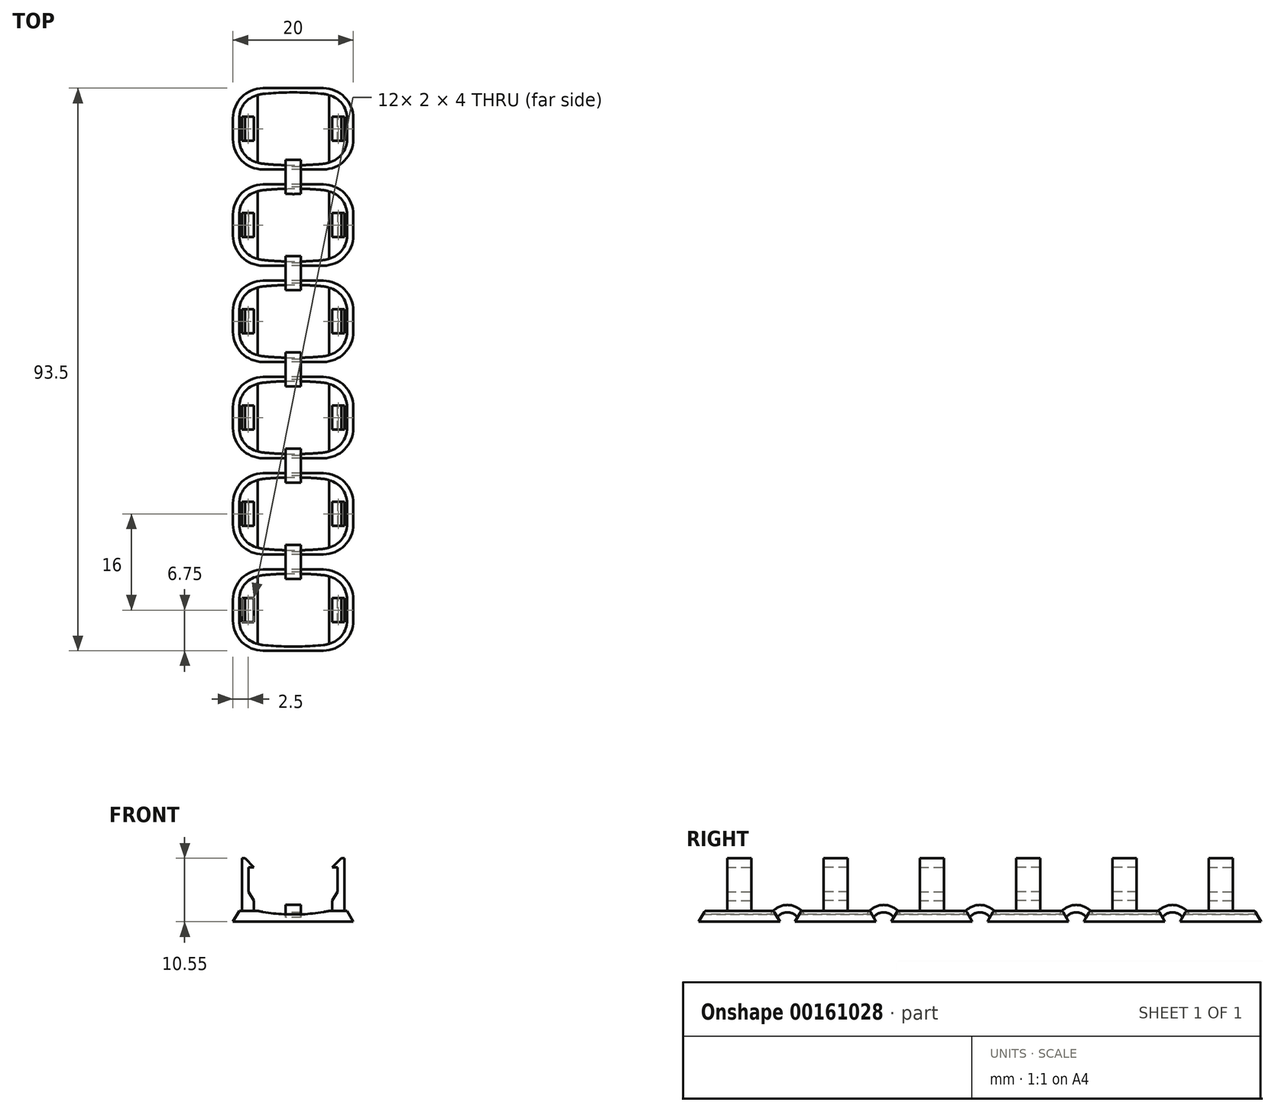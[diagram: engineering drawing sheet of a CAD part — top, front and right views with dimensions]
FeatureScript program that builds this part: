
annotation { "Feature Type Name" : "Feature", "Feature Type Description" : "" }
export const myFeature = defineFeature(function(context is Context, id is Id, definition is map)
    precondition{}
    {
        {
            var Q0;
            Q0=qCreatedBy(makeId("Top.planeOp"),FACE);
            var sketch = newSketch(context, id + "F0", { "sketchPlane" : qUnion([Q0])});
            skLineSegment(sketch, "E0.bottom", {"start": v(-5, 6.75) * mm, "end": v(5, 6.75) * mm});
            skLineSegment(sketch, "E0.top", {"start": v(-5, -6.75) * mm, "end": v(5, -6.75) * mm});
            skLineSegment(sketch, "E0.left", {"start": v(-10, 1.75) * mm, "end": v(-10, -1.75) * mm});
            skLineSegment(sketch, "E0.right", {"start": v(10, 1.75) * mm, "end": v(10, -1.75) * mm});
            skLineSegment(sketch, "E1", {"start": v(0, 21.6) * mm, "end": v(0, 6.75) * mm, "construction": true});
            skLineSegment(sketch, "E2", {"start": v(-21.62, 0) * mm, "end": v(-10, 0) * mm, "construction": true});
            skArc(sketch, "E3", {"start": v(-5, 6.75) * mm, "mid": v(-8.54, 5.29) * mm, "end": v(-10, 1.75) * mm});
            skArc(sketch, "E4", {"start": v(10, 1.75) * mm, "mid": v(8.54, 5.29) * mm, "end": v(5, 6.75) * mm});
            skArc(sketch, "E5", {"start": v(5, -6.75) * mm, "mid": v(8.54, -5.29) * mm, "end": v(10, -1.75) * mm});
            skPoint(sketch, "E6.orphan", {"position": v(10, 6.75) * mm});
            skArc(sketch, "E7.trimOffspring", {"start": v(-10, -1.75) * mm, "mid": v(-8.54, -5.29) * mm, "end": v(-5, -6.75) * mm});
            skLineSegment(sketch, "E8.trimOffspring", {"start": v(10, 0) * mm, "end": v(28.3, 0) * mm, "construction": true});
            skLineSegment(sketch, "E9.trimOffspring", {"start": v(0, -6.75) * mm, "end": v(0, -26.74) * mm, "construction": true});
            skSolve(sketch);
        }
        {
            var Q0;
            Q0=makeQuery(id+"F0.imprint","IMPRINT",FACE,{"disambiguationData":[TD([[makeQuery(id+"F0.imprint","IMPRINT",EDGE,{"derivedFrom":sQuery(id+"F0.wireOp",EDGE,"E0.bottom")}),-1.0]])]});
            extrude(context, id + "F1", {"entities" : qUnion([Q0]), "depth" : 1.8 * mm});
        }
        {
            var Q0;
            Q0=makeQuery(id+"F1.opExtrude","CAP_EDGE",EDGE,{"disambiguationData":[OSD([sQuery(id+"F0.wireOp",EDGE,"E0.top")])],"isStart":false});
            var Q1;
            Q1=makeQuery(id+"F1.opExtrude","CAP_EDGE",EDGE,{"disambiguationData":[OSD([sQuery(id+"F0.wireOp",EDGE,"E7.trimOffspring")])],"isStart":false});
            var Q2;
            Q2=makeQuery(id+"F1.opExtrude","CAP_EDGE",EDGE,{"disambiguationData":[OSD([sQuery(id+"F0.wireOp",EDGE,"E0.right")])],"isStart":false});
            var Q3;
            Q3=makeQuery(id+"F1.opExtrude","CAP_EDGE",EDGE,{"disambiguationData":[OSD([sQuery(id+"F0.wireOp",EDGE,"E5")])],"isStart":false});
            var Q4;
            Q4=makeQuery(id+"F1.opExtrude","CAP_EDGE",EDGE,{"disambiguationData":[OSD([sQuery(id+"F0.wireOp",EDGE,"E4")])],"isStart":false});
            var Q5;
            Q5=makeQuery(id+"F1.opExtrude","CAP_EDGE",EDGE,{"disambiguationData":[OSD([sQuery(id+"F0.wireOp",EDGE,"E0.bottom")])],"isStart":false});
            var Q6;
            Q6=makeQuery(id+"F1.opExtrude","CAP_EDGE",EDGE,{"disambiguationData":[OSD([sQuery(id+"F0.wireOp",EDGE,"E3")])],"isStart":false});
            var Q7;
            Q7=makeQuery(id+"F1.opExtrude","CAP_EDGE",EDGE,{"disambiguationData":[OSD([sQuery(id+"F0.wireOp",EDGE,"E0.left")])],"isStart":false});
            chamfer(context, id + "F2", {"entities" : qUnion([Q0, Q1, Q2, Q3, Q4, Q5, Q6, Q7]), "chamferType" : ChamferType.OFFSET_ANGLE, "width" : 1.04 * mm, "oppositeDirection" : false, "angle" : 60 * degree, "tangentPropagation" : true});
        }
        {
            var Q0;
            Q0=qCreatedBy(makeId("Front.planeOp"),FACE);
            var sketch = newSketch(context, id + "F3", { "sketchPlane" : qUnion([Q0])});
            skLineSegment(sketch, "E10", {"start": v(-6, 4.57) * mm, "end": v(-6, -3.38) * mm, "construction": true});
            skLineSegment(sketch, "E11", {"start": v(6, 4.53) * mm, "end": v(6, -3.32) * mm, "construction": true});
            skLineSegment(sketch, "E12", {"start": v(-10.74, 1.2) * mm, "end": v(11.87, 1.2) * mm, "construction": true});
            skArc(sketch, "E13", {"start": v(-6, 1.83) * mm, "mid": v(0, 1.2) * mm, "end": v(6, 1.8) * mm});
            skLineSegment(sketch, "E14", {"start": v(-6, 1.83) * mm, "end": v(-6, 3.37) * mm});
            skLineSegment(sketch, "E15", {"start": v(-6, 3.37) * mm, "end": v(6, 3.37) * mm});
            skLineSegment(sketch, "E16", {"start": v(6, 3.37) * mm, "end": v(6, 1.8) * mm});
            skSolve(sketch);
        }
        {
            var Q0;
            Q0 = qSketchRegion(id + "F3", true);
            extrude(context, id + "F4", {"entities" : qUnion([Q0]), "operationType" : NewBodyOperationType.REMOVE, "endBound" : BoundingType.SYMMETRIC, "oppositeDirection" : true, "depth" : 25 * mm});
        }
        {
            var Q0;
            Q0=qCreatedBy(makeId("Front.planeOp"),FACE);
            var sketch = newSketch(context, id + "F5", { "sketchPlane" : qUnion([Q0])});
            skLineSegment(sketch, "E17", {"start": v(-8.5, 11.85) * mm, "end": v(-8.5, 10.55) * mm, "construction": true});
            skLineSegment(sketch, "E18", {"start": v(8.5, 11.72) * mm, "end": v(8.5, -3.28) * mm, "construction": true});
            skLineSegment(sketch, "E19", {"start": v(-6.5, 11.8) * mm, "end": v(-6.5, -3.2) * mm, "construction": true});
            skLineSegment(sketch, "E20", {"start": v(6.5, 11.8) * mm, "end": v(6.5, -3.2) * mm, "construction": true});
            skLineSegment(sketch, "E21", {"start": v(-10.2, 10.55) * mm, "end": v(9.76, 10.55) * mm, "construction": true});
            skLineSegment(sketch, "E22", {"start": v(-11.42, 3.5) * mm, "end": v(12.16, 3.5) * mm, "construction": true});
            skLineSegment(sketch, "E23", {"start": v(-11.49, 5) * mm, "end": v(12.2, 5) * mm, "construction": true});
            skLineSegment(sketch, "E24", {"start": v(-7.4, 11.84) * mm, "end": v(-7.4, -3.13) * mm, "construction": true});
            skLineSegment(sketch, "E25", {"start": v(7.4, 11.66) * mm, "end": v(7.4, -3.03) * mm, "construction": true});
            skLineSegment(sketch, "E26", {"start": v(-11.03, 9.05) * mm, "end": v(14.92, 9.05) * mm, "construction": true});
            skLineSegment(sketch, "E27.top", {"start": v(-8.5, 10.55) * mm, "end": v(-8.5, 10.55) * mm});
            skLineSegment(sketch, "E28.trimOffspring", {"start": v(-8.5, 1.8) * mm, "end": v(-8.5, -3.15) * mm, "construction": true});
            skLineSegment(sketch, "E29", {"start": v(-8.5, 10.55) * mm, "end": v(-8.5, 1.8) * mm, "construction": true});
            skLineSegment(sketch, "E30", {"start": v(-8.5, 1.8) * mm, "end": v(-8.5, 10.55) * mm});
            skLineSegment(sketch, "E31", {"start": v(-8.5, 10.55) * mm, "end": v(-8, 10.55) * mm});
            skLineSegment(sketch, "E32", {"start": v(-6.5, 9.05) * mm, "end": v(-7.4, 9.05) * mm});
            skLineSegment(sketch, "E33", {"start": v(-7.4, 9.05) * mm, "end": v(-6.5, 9.05) * mm});
            skLineSegment(sketch, "E34", {"start": v(-7.4, 9.05) * mm, "end": v(-7.4, 5) * mm});
            skLineSegment(sketch, "E35", {"start": v(-7.4, 5) * mm, "end": v(-6.5, 3.5) * mm});
            skLineSegment(sketch, "E36", {"start": v(-6.5, 3.5) * mm, "end": v(-6.5, 1.79) * mm});
            skLineSegment(sketch, "E37", {"start": v(-6.5, 1.79) * mm, "end": v(-8.5, 1.8) * mm});
            skLineSegment(sketch, "E38", {"start": v(6.5, 1.8) * mm, "end": v(6.5, 3.5) * mm});
            skLineSegment(sketch, "E39", {"start": v(6.5, 3.5) * mm, "end": v(7.4, 5) * mm});
            skLineSegment(sketch, "E40", {"start": v(7.4, 5) * mm, "end": v(7.4, 9.05) * mm});
            skLineSegment(sketch, "E41", {"start": v(7.4, 9.05) * mm, "end": v(6.5, 9.05) * mm});
            skLineSegment(sketch, "E42", {"start": v(6.5, 9.05) * mm, "end": v(8, 10.55) * mm});
            skLineSegment(sketch, "E43", {"start": v(8, 10.55) * mm, "end": v(8.5, 10.55) * mm});
            skLineSegment(sketch, "E44", {"start": v(8.5, 10.55) * mm, "end": v(8.5, 1.8) * mm});
            skLineSegment(sketch, "E45", {"start": v(8.5, 1.8) * mm, "end": v(6.5, 1.8) * mm});
            skLineSegment(sketch, "E46", {"start": v(-8, 10.55) * mm, "end": v(-6.5, 9.05) * mm});
            skSolve(sketch);
        }
        {
            var Q0;
            Q0 = qSketchRegion(id + "F5", true);
            extrude(context, id + "F6", {"entities" : qUnion([Q0]), "operationType" : NewBodyOperationType.ADD, "endBound" : BoundingType.SYMMETRIC, "depth" : 4 * mm});
        }
        {
            var Q0;
            Q0=qCreatedBy(makeId("Front.planeOp"),FACE);
            cPlane(context, id + "F7", {"entities" : qUnion([Q0]), "cplaneType" : CPlaneType.OFFSET, "offset" : 8 * mm, "width" : 150 * mm, "height" : 150 * mm});
        }
        {
            var Q0;
            Q0=makeQuery(id+"F1.opExtrude","SWEPT_BODY",BODY,{"disambiguationData":[OSD([sQuery(id+"F0.wireOp",EDGE,"E0.bottom"),sQuery(id+"F0.wireOp",EDGE,"E0.top"),sQuery(id+"F0.wireOp",EDGE,"E0.left"),sQuery(id+"F0.wireOp",EDGE,"E0.right"),sQuery(id+"F0.wireOp",EDGE,"E3"),sQuery(id+"F0.wireOp",EDGE,"E4"),sQuery(id+"F0.wireOp",EDGE,"E5"),sQuery(id+"F0.wireOp",EDGE,"E7.trimOffspring")])]});
            var Q1;
            Q1=qCreatedBy(id+"F7.planeOp",FACE);
            mirror(context, id + "F8", {"entities" : qUnion([Q0]), "mirrorPlane" : qUnion([Q1])});
        }
        {
            var Q0;
            Q0=qCreatedBy(id+"F7.planeOp",FACE);
            cPlane(context, id + "F9", {"entities" : qUnion([Q0]), "cplaneType" : CPlaneType.OFFSET, "offset" : 16 * mm, "width" : 150 * mm, "height" : 150 * mm});
        }
        {
            var Q0;
            Q0=makeQuery(id+"F8.opPattern","COPY",BODY,{"derivedFrom":makeQuery(id+"F1.opExtrude","SWEPT_BODY",BODY,{"disambiguationData":[OSD([sQuery(id+"F0.wireOp",EDGE,"E0.bottom"),sQuery(id+"F0.wireOp",EDGE,"E0.top"),sQuery(id+"F0.wireOp",EDGE,"E0.left"),sQuery(id+"F0.wireOp",EDGE,"E0.right"),sQuery(id+"F0.wireOp",EDGE,"E3"),sQuery(id+"F0.wireOp",EDGE,"E4"),sQuery(id+"F0.wireOp",EDGE,"E5"),sQuery(id+"F0.wireOp",EDGE,"E7.trimOffspring")])]}),"instanceName":"1"});
            var Q1;
            Q1=qCreatedBy(id+"F9.planeOp",FACE);
            mirror(context, id + "F10", {"entities" : qUnion([Q0]), "mirrorPlane" : qUnion([Q1])});
        }
        {
            var Q0;
            Q0=qCreatedBy(makeId("Front.planeOp"),FACE);
            cPlane(context, id + "F11", {"entities" : qUnion([Q0]), "cplaneType" : CPlaneType.OFFSET, "offset" : 8 * mm, "oppositeDirection" : true, "width" : 150 * mm, "height" : 150 * mm});
        }
        {
            var Q0;
            Q0=makeQuery(id+"F1.opExtrude","SWEPT_BODY",BODY,{"disambiguationData":[OSD([sQuery(id+"F0.wireOp",EDGE,"E0.bottom"),sQuery(id+"F0.wireOp",EDGE,"E0.top"),sQuery(id+"F0.wireOp",EDGE,"E0.left"),sQuery(id+"F0.wireOp",EDGE,"E0.right"),sQuery(id+"F0.wireOp",EDGE,"E3"),sQuery(id+"F0.wireOp",EDGE,"E4"),sQuery(id+"F0.wireOp",EDGE,"E5"),sQuery(id+"F0.wireOp",EDGE,"E7.trimOffspring")])]});
            var Q1;
            Q1=makeQuery(id+"F8.opPattern","COPY",BODY,{"derivedFrom":makeQuery(id+"F1.opExtrude","SWEPT_BODY",BODY,{"disambiguationData":[OSD([sQuery(id+"F0.wireOp",EDGE,"E0.bottom"),sQuery(id+"F0.wireOp",EDGE,"E0.top"),sQuery(id+"F0.wireOp",EDGE,"E0.left"),sQuery(id+"F0.wireOp",EDGE,"E0.right"),sQuery(id+"F0.wireOp",EDGE,"E3"),sQuery(id+"F0.wireOp",EDGE,"E4"),sQuery(id+"F0.wireOp",EDGE,"E5"),sQuery(id+"F0.wireOp",EDGE,"E7.trimOffspring")])]}),"instanceName":"1"});
            var Q2;
            Q2=makeQuery(id+"F10.opPattern","COPY",BODY,{"derivedFrom":makeQuery(id+"F1.opExtrude","SWEPT_BODY",BODY,{"disambiguationData":[OSD([sQuery(id+"F0.wireOp",EDGE,"E0.bottom"),sQuery(id+"F0.wireOp",EDGE,"E0.top"),sQuery(id+"F0.wireOp",EDGE,"E0.left"),sQuery(id+"F0.wireOp",EDGE,"E0.right"),sQuery(id+"F0.wireOp",EDGE,"E3"),sQuery(id+"F0.wireOp",EDGE,"E4"),sQuery(id+"F0.wireOp",EDGE,"E5"),sQuery(id+"F0.wireOp",EDGE,"E7.trimOffspring")])]}),"instanceName":"1"});
            var Q3;
            Q3=makeQuery(id+"F10.opPattern","COPY",BODY,{"derivedFrom":makeQuery(id+"F8.opPattern","COPY",BODY,{"derivedFrom":makeQuery(id+"F1.opExtrude","SWEPT_BODY",BODY,{"disambiguationData":[OSD([sQuery(id+"F0.wireOp",EDGE,"E0.bottom"),sQuery(id+"F0.wireOp",EDGE,"E0.top"),sQuery(id+"F0.wireOp",EDGE,"E0.left"),sQuery(id+"F0.wireOp",EDGE,"E0.right"),sQuery(id+"F0.wireOp",EDGE,"E3"),sQuery(id+"F0.wireOp",EDGE,"E4"),sQuery(id+"F0.wireOp",EDGE,"E5"),sQuery(id+"F0.wireOp",EDGE,"E7.trimOffspring")])]}),"instanceName":"1"}),"instanceName":"1"});
            var Q4;
            Q4=qCreatedBy(id+"F11.planeOp",FACE);
            mirror(context, id + "F12", {"entities" : qUnion([Q0, Q1, Q2, Q3]), "mirrorPlane" : qUnion([Q4])});
        }
        {
            var Q0;
            Q0=qCreatedBy(makeId("Right.planeOp"),FACE);
            var sketch = newSketch(context, id + "F13", { "sketchPlane" : qUnion([Q0])});
            skLineSegment(sketch, "E47", {"start": v(-11.94, 1.3) * mm, "end": v(-4.48, 1.3) * mm, "construction": true});
            skArc(sketch, "E48", {"start": v(-5.04, 1) * mm, "mid": v(-8.25, 2.78) * mm, "end": v(-11.15, 0.53) * mm});
            skArc(sketch, "E49", {"start": v(-6.16, 0.47) * mm, "mid": v(-8.1, 1.56) * mm, "end": v(-9.93, 0.27) * mm});
            skLineSegment(sketch, "E50", {"start": v(-11.15, 0.53) * mm, "end": v(-9.93, 0.27) * mm});
            skLineSegment(sketch, "E51", {"start": v(-6.16, 0.47) * mm, "end": v(-5.04, 1) * mm});
            skSolve(sketch);
        }
        {
            var Q0;
            Q0 = qSketchRegion(id + "F13", true);
            extrude(context, id + "F14", {"entities" : qUnion([Q0]), "operationType" : NewBodyOperationType.ADD, "endBound" : BoundingType.SYMMETRIC, "depth" : 2.5 * mm});
        }
        {
            var Q0;
            Q0=makeQuery(id+"F1.opExtrude","SWEPT_BODY",BODY,{"disambiguationData":[OSD([sQuery(id+"F0.wireOp",EDGE,"E0.bottom"),sQuery(id+"F0.wireOp",EDGE,"E0.top"),sQuery(id+"F0.wireOp",EDGE,"E0.left"),sQuery(id+"F0.wireOp",EDGE,"E0.right"),sQuery(id+"F0.wireOp",EDGE,"E3"),sQuery(id+"F0.wireOp",EDGE,"E4"),sQuery(id+"F0.wireOp",EDGE,"E5"),sQuery(id+"F0.wireOp",EDGE,"E7.trimOffspring")])]});
            var Q1;
            Q1=qCreatedBy(makeId("Front.planeOp"),FACE);
            mirror(context, id + "F15", {"entities" : qUnion([Q0]), "mirrorPlane" : qUnion([Q1])});
        }
        {
            var Q0;
            Q0=qCreatedBy(id+"F7.planeOp",FACE);
            cPlane(context, id + "F16", {"entities" : qUnion([Q0]), "cplaneType" : CPlaneType.OFFSET, "offset" : 8 * mm, "width" : 150 * mm, "height" : 150 * mm});
        }
        {
            var Q0;
            Q0=makeQuery(id+"F1.opExtrude","SWEPT_BODY",BODY,{"disambiguationData":[OSD([sQuery(id+"F0.wireOp",EDGE,"E0.bottom"),sQuery(id+"F0.wireOp",EDGE,"E0.top"),sQuery(id+"F0.wireOp",EDGE,"E0.left"),sQuery(id+"F0.wireOp",EDGE,"E0.right"),sQuery(id+"F0.wireOp",EDGE,"E3"),sQuery(id+"F0.wireOp",EDGE,"E4"),sQuery(id+"F0.wireOp",EDGE,"E5"),sQuery(id+"F0.wireOp",EDGE,"E7.trimOffspring")])]});
            var Q1;
            Q1=qCreatedBy(id+"F16.planeOp",FACE);
            mirror(context, id + "F17", {"entities" : qUnion([Q0]), "mirrorPlane" : qUnion([Q1])});
        }
        {
            var Q0;
            Q0=qCreatedBy(id+"F11.planeOp",FACE);
            cPlane(context, id + "F18", {"entities" : qUnion([Q0]), "cplaneType" : CPlaneType.OFFSET, "offset" : 8 * mm, "oppositeDirection" : true, "width" : 150 * mm, "height" : 150 * mm});
        }
        {
            var Q0;
            Q0=makeQuery(id+"F15.opPattern","COPY",BODY,{"derivedFrom":makeQuery(id+"F1.opExtrude","SWEPT_BODY",BODY,{"disambiguationData":[OSD([sQuery(id+"F0.wireOp",EDGE,"E0.bottom"),sQuery(id+"F0.wireOp",EDGE,"E0.top"),sQuery(id+"F0.wireOp",EDGE,"E0.left"),sQuery(id+"F0.wireOp",EDGE,"E0.right"),sQuery(id+"F0.wireOp",EDGE,"E3"),sQuery(id+"F0.wireOp",EDGE,"E4"),sQuery(id+"F0.wireOp",EDGE,"E5"),sQuery(id+"F0.wireOp",EDGE,"E7.trimOffspring")])]}),"instanceName":"1"});
            var Q1;
            Q1=makeQuery(id+"F1.opExtrude","SWEPT_BODY",BODY,{"disambiguationData":[OSD([sQuery(id+"F0.wireOp",EDGE,"E0.bottom"),sQuery(id+"F0.wireOp",EDGE,"E0.top"),sQuery(id+"F0.wireOp",EDGE,"E0.left"),sQuery(id+"F0.wireOp",EDGE,"E0.right"),sQuery(id+"F0.wireOp",EDGE,"E3"),sQuery(id+"F0.wireOp",EDGE,"E4"),sQuery(id+"F0.wireOp",EDGE,"E5"),sQuery(id+"F0.wireOp",EDGE,"E7.trimOffspring")])]});
            var Q2;
            Q2=qCreatedBy(id+"F18.planeOp",FACE);
            mirror(context, id + "F19", {"entities" : qUnion([Q0, Q1]), "mirrorPlane" : qUnion([Q2])});
        }
    });
